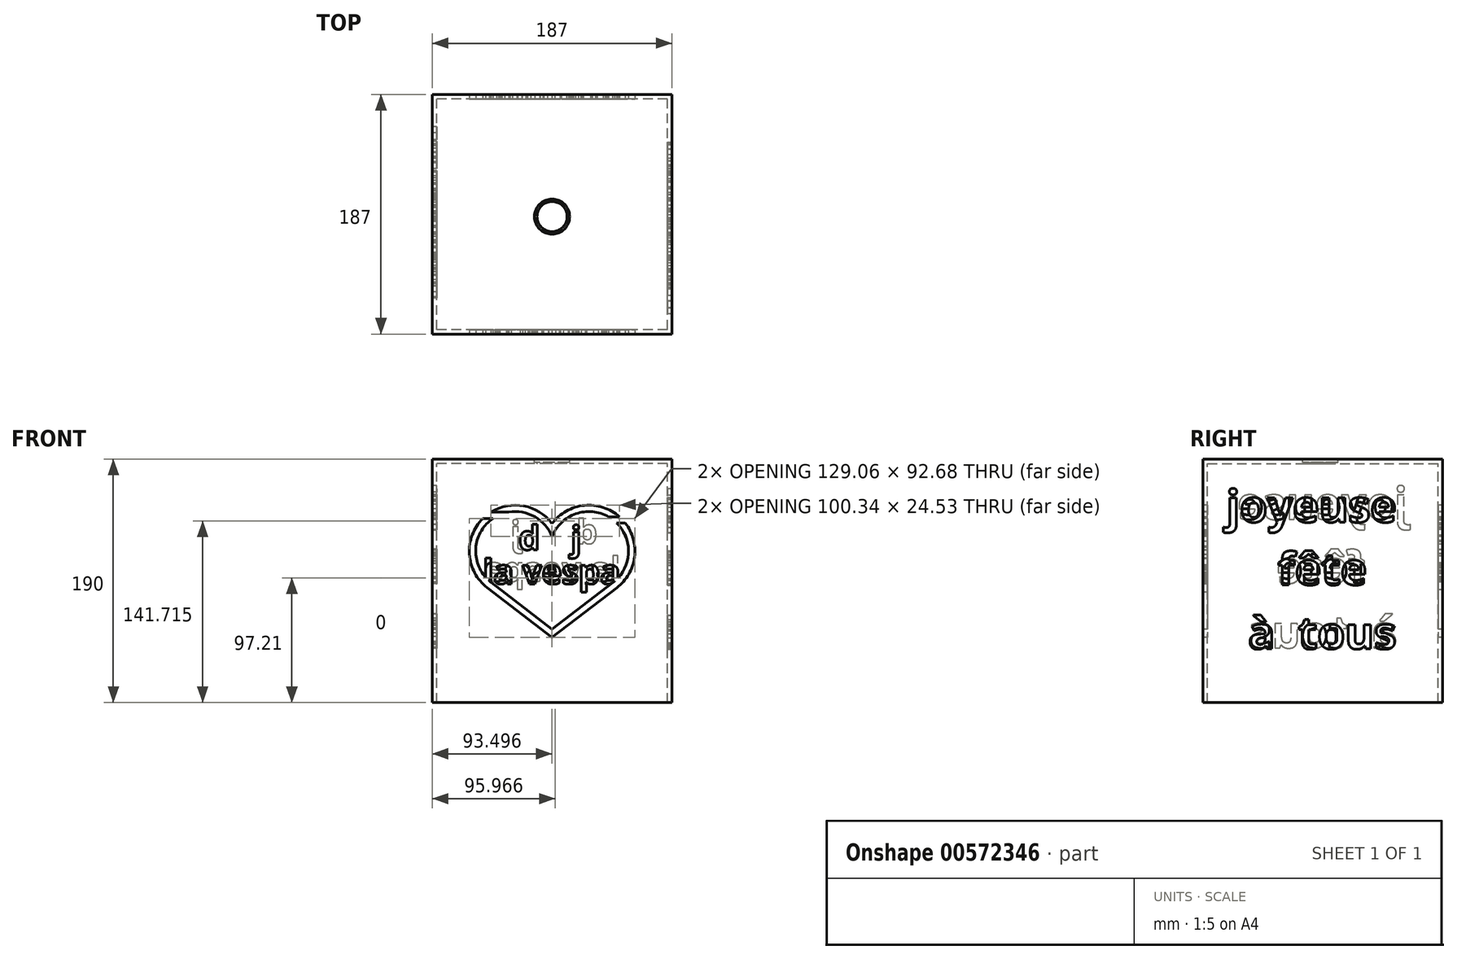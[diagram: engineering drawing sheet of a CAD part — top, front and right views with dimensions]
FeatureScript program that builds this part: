
annotation { "Feature Type Name" : "Feature", "Feature Type Description" : "" }
export const myFeature = defineFeature(function(context is Context, id is Id, definition is map)
    precondition{}
    {
        {
            var Q0;
            Q0=qCreatedBy(makeId("Top.planeOp"),FACE);
            var sketch = newSketch(context, id + "F0", { "sketchPlane" : qUnion([Q0])});
            skLineSegment(sketch, "E0.bottom", {"start": v(-93.5, 95.35) * mm, "end": v(93.5, 95.35) * mm});
            skLineSegment(sketch, "E0.top", {"start": v(-93.5, -91.65) * mm, "end": v(93.5, -91.65) * mm});
            skLineSegment(sketch, "E0.left", {"start": v(-93.5, 95.35) * mm, "end": v(-93.5, -91.65) * mm});
            skLineSegment(sketch, "E0.right", {"start": v(93.5, 95.35) * mm, "end": v(93.5, -91.65) * mm});
            skSolve(sketch);
        }
        {
            var Q0;
            Q0=makeQuery(id+"F0.imprint","IMPRINT",FACE,{"disambiguationData":[TD([[makeQuery(id+"F0.imprint","IMPRINT",EDGE,{"derivedFrom":sQuery(id+"F0.wireOp",EDGE,"E0.bottom")}),-1.0]])]});
            extrude(context, id + "F1", {"entities" : qUnion([Q0]), "depth" : 190 * mm, "offsetDistance" : 25 * mm});
        }
        {
            var Q0;
            Q0=makeQuery(id+"F1.opExtrude","CAP_FACE",FACE,{"disambiguationData":[OSD([sQuery(id+"F0.wireOp",EDGE,"E0.bottom"),sQuery(id+"F0.wireOp",EDGE,"E0.top"),sQuery(id+"F0.wireOp",EDGE,"E0.left"),sQuery(id+"F0.wireOp",EDGE,"E0.right")])],"isStart":false});
            var sketch = newSketch(context, id + "F2", { "sketchPlane" : qUnion([Q0])});
            skLineSegment(sketch, "E1.0", {"start": v(-93.5, 91.85) * mm, "end": v(93.5, 91.85) * mm});
            skLineSegment(sketch, "E2.0", {"start": v(90, 95.35) * mm, "end": v(90, -91.65) * mm});
            skLineSegment(sketch, "E3.0", {"start": v(-93.5, -88.15) * mm, "end": v(93.5, -88.15) * mm});
            skLineSegment(sketch, "E4.0", {"start": v(-90, 95.35) * mm, "end": v(-90, -91.65) * mm});
            skSolve(sketch);
        }
        {
            var Q0;
            {var subQ0=sQuery(id+"F2.wireOp",EDGE,"E4.0");var subQ1=sQuery(id+"F2.wireOp",EDGE,"E1.0");var subQ2=makeQuery(id+"F2.imprint","INTERSECT",VERTEX,{"derivedFrom":[subQ1,subQ0]});Q0=makeQuery(id+"F2.imprint","IMPRINT",FACE,{"disambiguationData":[TD([[makeQuery(id+"F2.imprint","IMPRINT",EDGE,{"disambiguationData":[TD([[subQ2,-1.0]])],"derivedFrom":subQ1}),-1.0]])]});}
            extrude(context, id + "F3", {"entities" : qUnion([Q0]), "operationType" : NewBodyOperationType.REMOVE, "oppositeDirection" : true, "depth" : 190 * mm, "offsetDistance" : 25 * mm});
        }
        {
            var Q0;
            Q0=makeQuery(id+"F1.opExtrude","SWEPT_FACE",FACE,{"disambiguationData":[OSD([sQuery(id+"F0.wireOp",EDGE,"E0.right")])]});
            var sketch = newSketch(context, id + "F4", { "sketchPlane" : qUnion([Q0])});
            skText(sketch, "E5", { "text": "joyeuse", "fontName": "OpenSans-Bold.ttf"});
            skText(sketch, "E6", { "text": "fête", "fontName": "OpenSans-Bold.ttf"});
            skText(sketch, "E7", { "text": "à  tous", "fontName": "OpenSans-Bold.ttf"});
            const initialGuessF4  = {"E5": [-0.0735, 0.14072, 1, 0, 0.025], "E6": [-0.0333, 0.09183, 1, 0, 0.025], "E7": [-0.05645, 0.04183, 1, 0, 0.025]};
            skSetInitialGuess(sketch, initialGuessF4);
            skSolve(sketch);
        }
        {
            var Q0;
            Q0=makeQuery(id+"F1.opExtrude","SWEPT_FACE",FACE,{"disambiguationData":[OSD([sQuery(id+"F0.wireOp",EDGE,"E0.left")])]});
            var sketch = newSketch(context, id + "F5", { "sketchPlane" : qUnion([Q0])});
            skText(sketch, "E8", { "text": "joyeuse", "fontName": "OpenSans-Bold.ttf"});
            skText(sketch, "E9", { "text": "fête", "fontName": "OpenSans-Bold.ttf"});
            skText(sketch, "E10", { "text": "à  tous", "fontName": "OpenSans-Bold.ttf"});
            const initialGuessF5  = {"E8": [-0.06797, 0.14293, 1, 0, 0.025], "E9": [-0.03515, 0.0931, 1, 0, 0.025], "E10": [-0.06016, 0.04266, 1, 0, 0.025]};
            skSetInitialGuess(sketch, initialGuessF5);
            skSolve(sketch);
        }
        {
            var Q0;
            Q0=qSketchRegion(id+"F5",true);
            var Q1;
            Q1=qSketchRegion(id+"F4",true);
            var Q2;
            Q2=qSketchRegion(id+"FytjR2NVyljPgOM_1",true);
            extrude(context, id + "F6", {"entities" : qUnion([Q0, Q1, Q2]), "operationType" : NewBodyOperationType.REMOVE, "oppositeDirection" : true, "depth" : 3.5 * mm, "offsetDistance" : 25 * mm});
        }
        {
            var Q0;
            Q0 = qSketchRegion(id + "F4", true);
            extrude(context, id + "F7", {"entities" : qUnion([Q0]), "operationType" : NewBodyOperationType.REMOVE, "oppositeDirection" : true, "depth" : 3.5 * mm, "offsetDistance" : 25 * mm});
        }
        {
            var Q0;
            Q0=makeQuery(id+"F1.opExtrude","SWEPT_FACE",FACE,{"disambiguationData":[OSD([sQuery(id+"F0.wireOp",EDGE,"E0.top")])]});
            var sketch = newSketch(context, id + "F8", { "sketchPlane" : qUnion([Q0])});
            skLineSegment(sketch, "E11", {"start": v(0, 0) * mm, "end": v(0, 190) * mm, "construction": true});
            skArc(sketch, "E12", {"start": v(0, 139.6) * mm, "mid": v(-22.11, 153.36) * mm, "end": v(-47.7, 148.55) * mm});
            skLineSegment(sketch, "E13", {"start": v(-50.55, 89.6) * mm, "end": v(0, 50.87) * mm});
            skArc(sketch, "E14.MirrorCS", {"start": v(0, 139.6) * mm, "mid": v(25.17, 153.8) * mm, "end": v(52.64, 144.85) * mm});
            skLineSegment(sketch, "E15.MirrorCS", {"start": v(50.55, 89.6) * mm, "end": v(0, 50.87) * mm});
            skLineSegment(sketch, "E16.0", {"start": v(-47.5, 93.57) * mm, "end": v(0, 57.17) * mm});
            skArc(sketch, "E16.1", {"start": v(0, 129.45) * mm, "mid": v(-13.55, 145) * mm, "end": v(-33.86, 148.55) * mm});
            skArc(sketch, "E16.2", {"start": v(0, 129.45) * mm, "mid": v(18.55, 147.25) * mm, "end": v(44.15, 144.85) * mm});
            skLineSegment(sketch, "E16.3", {"start": v(47.5, 93.57) * mm, "end": v(0, 57.17) * mm});
            skLineSegment(sketch, "E17.bottom", {"start": v(-47.7, 148.55) * mm, "end": v(-33.86, 148.55) * mm});
            skLineSegment(sketch, "E17.top", {"start": v(-54.02, 143.55) * mm, "end": v(-46.21, 143.55) * mm});
            skArc(sketch, "E18.trimOffspring", {"start": v(-54.02, 143.55) * mm, "mid": v(-64.54, 115.79) * mm, "end": v(-50.55, 89.6) * mm});
            skArc(sketch, "E19.trimOffspring", {"start": v(-46.21, 143.55) * mm, "mid": v(-59.6, 118.89) * mm, "end": v(-47.5, 93.57) * mm});
            skLineSegment(sketch, "E20.bottom", {"start": v(44.15, 144.85) * mm, "end": v(52.64, 144.85) * mm});
            skLineSegment(sketch, "E20.top", {"start": v(50.44, 140.05) * mm, "end": v(57.1, 140.05) * mm});
            skArc(sketch, "E21.trimOffspring", {"start": v(50.44, 140.05) * mm, "mid": v(59.55, 116.15) * mm, "end": v(47.5, 93.57) * mm});
            skArc(sketch, "E22.trimOffspring", {"start": v(57.1, 140.05) * mm, "mid": v(64.31, 113.47) * mm, "end": v(50.55, 89.6) * mm});
            skSolve(sketch);
        }
        {
            var Q0;
            Q0 = qSketchRegion(id + "F8", true);
            extrude(context, id + "F9", {"entities" : qUnion([Q0]), "operationType" : NewBodyOperationType.REMOVE, "endBound" : BoundingType.THROUGH_ALL, "oppositeDirection" : true, "depth" : 25 * mm, "offsetDistance" : 25 * mm});
        }
        {
            var Q0;
            Q0=makeQuery(id+"F1.opExtrude","SWEPT_FACE",FACE,{"disambiguationData":[OSD([sQuery(id+"F0.wireOp",EDGE,"E0.bottom")])]});
            var sketch = newSketch(context, id + "F10", { "sketchPlane" : qUnion([Q0])});
            skText(sketch, "E23", { "text": "d", "fontName": "OpenSans-Bold.ttf"});
            skPoint(sketch, "E24", {"position": v(-35.5, 88.93) * mm});
            skText(sketch, "E25", { "text": "j", "fontName": "OpenSans-Bold.ttf"});
            skText(sketch, "E26", { "text": "la vespa", "fontName": "OpenSans-Bold.ttf"});
            const initialGuessF10  = {"E23": [-0.0355, 0.12398, 1, 0, 0.019], "E25": [0.02456, 0.12266, 1, 0, 0.019], "E26": [-0.05347, 0.09455, 1, 0, 0.019]};
            skSetInitialGuess(sketch, initialGuessF10);
            skSolve(sketch);
        }
        {
            var Q0;
            Q0=qSketchRegion(id+"F10",true);
            extrude(context, id + "F11", {"entities" : qUnion([Q0]), "operationType" : NewBodyOperationType.REMOVE, "oppositeDirection" : true, "depth" : 3.5 * mm, "offsetDistance" : 25 * mm});
        }
        {
            var Q0;
            Q0=makeQuery(id+"F1.opExtrude","SWEPT_FACE",FACE,{"disambiguationData":[OSD([sQuery(id+"F0.wireOp",EDGE,"E0.top")])]});
            var sketch = newSketch(context, id + "F12", { "sketchPlane" : qUnion([Q0])});
            skText(sketch, "E27", { "text": "d", "fontName": "OpenSans-Bold.ttf"});
            skPoint(sketch, "E28", {"position": v(-26.12, 68.56) * mm});
            skText(sketch, "E29", { "text": "j", "fontName": "OpenSans-Bold.ttf"});
            skText(sketch, "E30", { "text": "la vespa", "fontName": "OpenSans-Bold.ttf"});
            const initialGuessF12  = {"E27": [-0.02612, 0.11912, 1, 0, 0.019], "E29": [0.01477, 0.11862, 1, 0, 0.019], "E30": [-0.05387, 0.09255, 1, 0, 0.019]};
            skSetInitialGuess(sketch, initialGuessF12);
            skSolve(sketch);
        }
        {
            var Q0;
            Q0 = qSketchRegion(id + "F12", true);
            extrude(context, id + "F13", {"entities" : qUnion([Q0]), "operationType" : NewBodyOperationType.REMOVE, "oppositeDirection" : true, "depth" : 3.5 * mm, "offsetDistance" : 25 * mm});
        }
        {
            var Q0;
            Q0=makeQuery(id+"F1.opExtrude","CAP_FACE",FACE,{"disambiguationData":[OSD([sQuery(id+"F0.wireOp",EDGE,"E0.bottom"),sQuery(id+"F0.wireOp",EDGE,"E0.top"),sQuery(id+"F0.wireOp",EDGE,"E0.left"),sQuery(id+"F0.wireOp",EDGE,"E0.right")])],"isStart":false});
            var sketch = newSketch(context, id + "F14", { "sketchPlane" : qUnion([Q0])});
            skLineSegment(sketch, "E31.bottom", {"start": v(-93.5, 95.35) * mm, "end": v(93.5, 95.35) * mm});
            skLineSegment(sketch, "E31.top", {"start": v(-93.5, -91.65) * mm, "end": v(93.5, -91.65) * mm});
            skLineSegment(sketch, "E31.left", {"start": v(-93.5, 95.35) * mm, "end": v(-93.5, -91.65) * mm});
            skLineSegment(sketch, "E31.right", {"start": v(93.5, 95.35) * mm, "end": v(93.5, -91.65) * mm});
            skSolve(sketch);
        }
        {
            var Q0;
            Q0 = qSketchRegion(id + "F14", true);
            extrude(context, id + "F15", {"entities" : qUnion([Q0]), "operationType" : NewBodyOperationType.ADD, "oppositeDirection" : true, "depth" : 3.5 * mm, "offsetDistance" : 25 * mm});
        }
        {
            var Q0;
            Q0=makeQuery(id+"F15.boolean.opBoolean","MERGE",FACE,{"derivedFrom":[makeQuery(id+"F1.opExtrude","CAP_FACE",FACE,{"disambiguationData":[OSD([sQuery(id+"F0.wireOp",EDGE,"E0.bottom"),sQuery(id+"F0.wireOp",EDGE,"E0.top"),sQuery(id+"F0.wireOp",EDGE,"E0.left"),sQuery(id+"F0.wireOp",EDGE,"E0.right")])],"isStart":false}),makeQuery(id+"F15.opExtrude","CAP_FACE",FACE,{"disambiguationData":[OSD([sQuery(id+"F14.wireOp",EDGE,"E31.bottom"),sQuery(id+"F14.wireOp",EDGE,"E31.top"),sQuery(id+"F14.wireOp",EDGE,"E31.left"),sQuery(id+"F14.wireOp",EDGE,"E31.right")])],"isStart":true})]});
            var sketch = newSketch(context, id + "F16", { "sketchPlane" : qUnion([Q0])});
            skCircle(sketch, "E32", {"center": v(0, 0) * mm, "radius": 11.75 * mm});
            skSolve(sketch);
        }
        {
            var Q0;
            Q0 = qSketchRegion(id + "F16", true);
            extrude(context, id + "F17", {"entities" : qUnion([Q0]), "operationType" : NewBodyOperationType.REMOVE, "oppositeDirection" : true, "depth" : 25 * mm, "offsetDistance" : 25 * mm});
        }
        {
            var Q0;
            Q0=makeQuery(id+"F15.boolean.opBoolean","MERGE",FACE,{"derivedFrom":[makeQuery(id+"F1.opExtrude","CAP_FACE",FACE,{"disambiguationData":[OSD([sQuery(id+"F0.wireOp",EDGE,"E0.bottom"),sQuery(id+"F0.wireOp",EDGE,"E0.top"),sQuery(id+"F0.wireOp",EDGE,"E0.left"),sQuery(id+"F0.wireOp",EDGE,"E0.right")])],"isStart":false}),makeQuery(id+"F15.opExtrude","CAP_FACE",FACE,{"disambiguationData":[OSD([sQuery(id+"F14.wireOp",EDGE,"E31.bottom"),sQuery(id+"F14.wireOp",EDGE,"E31.top"),sQuery(id+"F14.wireOp",EDGE,"E31.left"),sQuery(id+"F14.wireOp",EDGE,"E31.right")])],"isStart":true})]});
            var sketch = newSketch(context, id + "F18", { "sketchPlane" : qUnion([Q0])});
            skCircle(sketch, "E33", {"center": v(0, 0) * mm, "radius": 13.75 * mm});
            skSolve(sketch);
        }
        {
            var Q0;
            Q0 = qSketchRegion(id + "F18", true);
            extrude(context, id + "F19", {"entities" : qUnion([Q0]), "operationType" : NewBodyOperationType.REMOVE, "oppositeDirection" : true, "depth" : 2.5 * mm, "offsetDistance" : 25 * mm});
        }
    });
